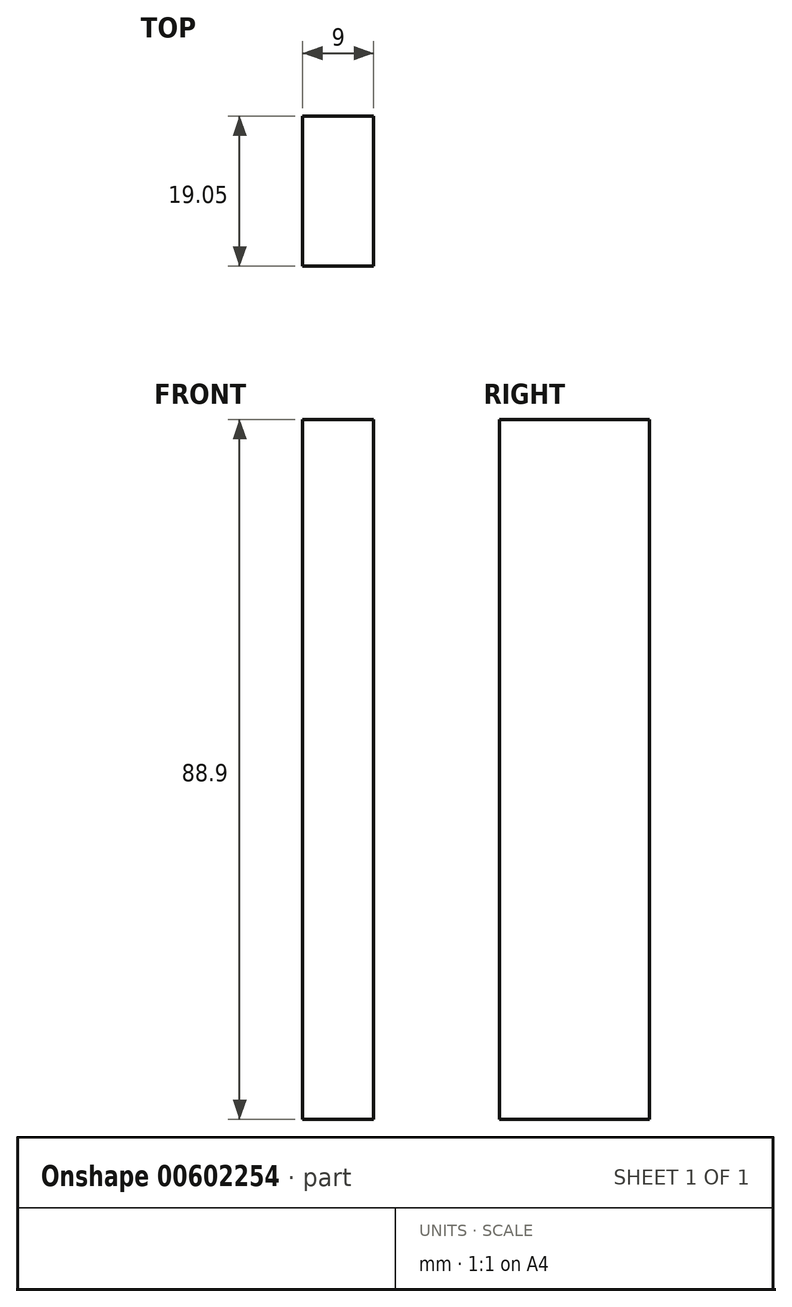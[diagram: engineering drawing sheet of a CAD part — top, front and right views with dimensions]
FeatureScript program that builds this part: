
annotation { "Feature Type Name" : "Feature", "Feature Type Description" : "" }
export const myFeature = defineFeature(function(context is Context, id is Id, definition is map)
    precondition{}
    {
        {
            assignVariable(context, id + "F0", {"name" : "largeur", "anyValue" : 9});
        }
        {
            var Q0;
            Q0=qCreatedBy(makeId("Right.planeOp"),FACE);
            var sketch = newSketch(context, id + "F1", { "sketchPlane" : qUnion([Q0])});
            skLineSegment(sketch, "E0.bottom", {"start": v(0, 0) * mm, "end": v(19.05, 0) * mm});
            skLineSegment(sketch, "E0.top", {"start": v(0, 88.9) * mm, "end": v(19.05, 88.9) * mm});
            skLineSegment(sketch, "E0.left", {"start": v(0, 0) * mm, "end": v(0, 88.9) * mm});
            skLineSegment(sketch, "E0.right", {"start": v(19.05, 0) * mm, "end": v(19.05, 88.9) * mm});
            skSolve(sketch);
        }
        {
            var Q0;
            Q0 = qSketchRegion(id + "F1", true);
            extrude(context, id + "F2", {"entities" : qUnion([Q0]), "oppositeDirection" : true, "depth" : (getVariable(context, 'largeur')) * mm, "offsetDistance" : 25.4 * mm});
        }
    });
